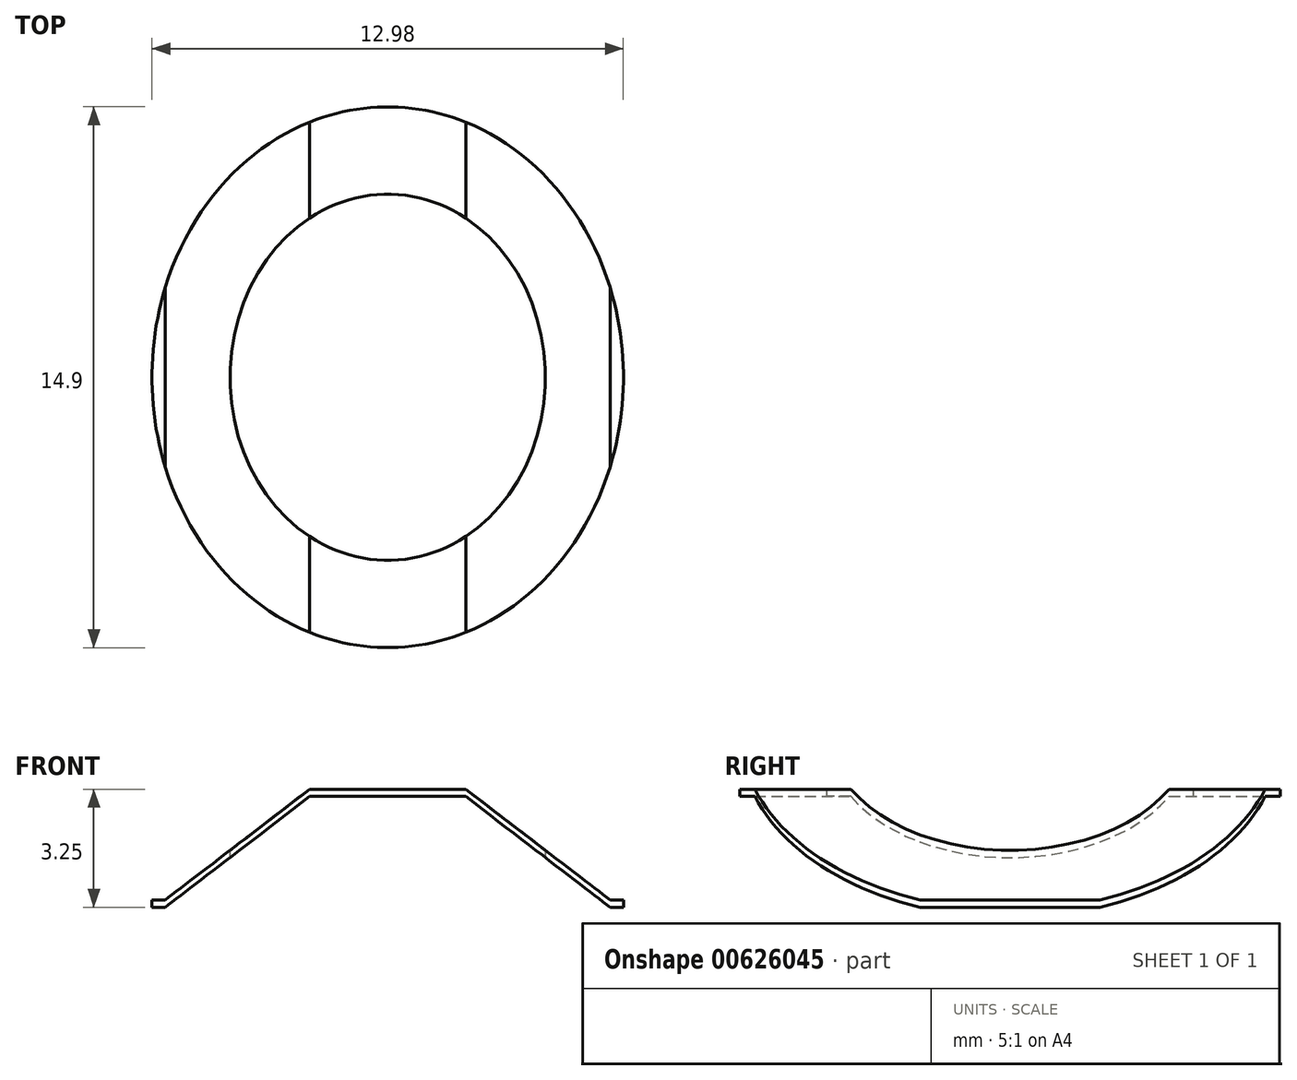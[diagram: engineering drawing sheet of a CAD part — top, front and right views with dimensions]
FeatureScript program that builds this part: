
annotation { "Feature Type Name" : "Feature", "Feature Type Description" : "" }
export const myFeature = defineFeature(function(context is Context, id is Id, definition is map)
    precondition{}
    {
        {
            var Q0;
            Q0=qCreatedBy(makeId("Front.planeOp"),FACE);
            var sketch = newSketch(context, id + "F0", { "sketchPlane" : qUnion([Q0])});
            skLineSegment(sketch, "E0", {"start": v(-7.32, 0) * mm, "end": v(-6.12, 0) * mm});
            skLineSegment(sketch, "E1", {"start": v(-6.12, 0) * mm, "end": v(-2.15, 3.05) * mm});
            skLineSegment(sketch, "E2", {"start": v(-2.15, 3.05) * mm, "end": v(2.15, 3.05) * mm});
            skLineSegment(sketch, "E3", {"start": v(2.15, 3.05) * mm, "end": v(6.12, 0) * mm});
            skLineSegment(sketch, "E4", {"start": v(6.12, 0) * mm, "end": v(7.32, 0) * mm});
            skLineSegment(sketch, "E5", {"start": v(-7.32, 0.2) * mm, "end": v(-6.12, 0.2) * mm});
            skLineSegment(sketch, "E6", {"start": v(-6.12, 0.2) * mm, "end": v(-2.15, 3.25) * mm});
            skLineSegment(sketch, "E7", {"start": v(-2.15, 3.25) * mm, "end": v(2.15, 3.25) * mm});
            skLineSegment(sketch, "E8", {"start": v(2.15, 3.25) * mm, "end": v(6.12, 0.2) * mm});
            skLineSegment(sketch, "E9", {"start": v(6.12, 0.2) * mm, "end": v(7.32, 0.2) * mm});
            skLineSegment(sketch, "E10", {"start": v(7.32, 0.2) * mm, "end": v(7.32, 0) * mm});
            skLineSegment(sketch, "E11", {"start": v(-7.32, 0.2) * mm, "end": v(-7.32, 0) * mm});
            skSolve(sketch);
        }
        {
            var Q0;
            Q0=makeQuery(id+"F0.imprint","IMPRINT",FACE,{"disambiguationData":[TD([[makeQuery(id+"F0.imprint","IMPRINT",EDGE,{"derivedFrom":sQuery(id+"F0.wireOp",EDGE,"E0")}),1.0]])]});
            extrude(context, id + "F1", {"entities" : qUnion([Q0]), "depth" : 14.9 * mm, "offsetDistance" : 25 * mm, "symmetric" : true});
        }
        {
            var Q0;
            Q0=qCreatedBy(makeId("Top.planeOp"),FACE);
            var sketch = newSketch(context, id + "F2", { "sketchPlane" : qUnion([Q0])});
            skEllipse(sketch, "E12", {"center": v(0, 0) * mm, "majorRadius": 5.05 * mm, "minorRadius": 4.35 * mm, "majorAxis": v(0, -1)});
            skEllipse(sketch, "E13", {"center": v(0, 0) * mm, "majorRadius": 7.45 * mm, "minorRadius": 6.5 * mm, "majorAxis": v(0, -1)});
            skLineSegment(sketch, "E14.bottom", {"start": v(-10.01, 8.79) * mm, "end": v(9.37, 8.79) * mm});
            skLineSegment(sketch, "E14.top", {"start": v(-10.01, -9.6) * mm, "end": v(9.37, -9.6) * mm});
            skLineSegment(sketch, "E14.left", {"start": v(-10.01, 8.79) * mm, "end": v(-10.01, -9.6) * mm});
            skLineSegment(sketch, "E14.right", {"start": v(9.37, 8.79) * mm, "end": v(9.37, -9.6) * mm});
            skSolve(sketch);
        }
        {
            var Q0;
            Q0=makeQuery(id+"F2.imprint","IMPRINT",FACE,{"disambiguationData":[TD([[makeQuery(id+"F2.imprint","IMPRINT",EDGE,{"derivedFrom":sQuery(id+"F2.wireOp",EDGE,"E12")}),1.0]])]});
            extrude(context, id + "F3", {"entities" : qUnion([Q0]), "operationType" : NewBodyOperationType.REMOVE, "depth" : 25 * mm, "offsetDistance" : 25 * mm});
        }
        {
            var Q0;
            Q0 = qSketchRegion(id + "F2", true);
            extrude(context, id + "F4", {"entities" : qUnion([Q0]), "operationType" : NewBodyOperationType.REMOVE, "depth" : 25 * mm, "offsetDistance" : 25 * mm});
        }
    });
